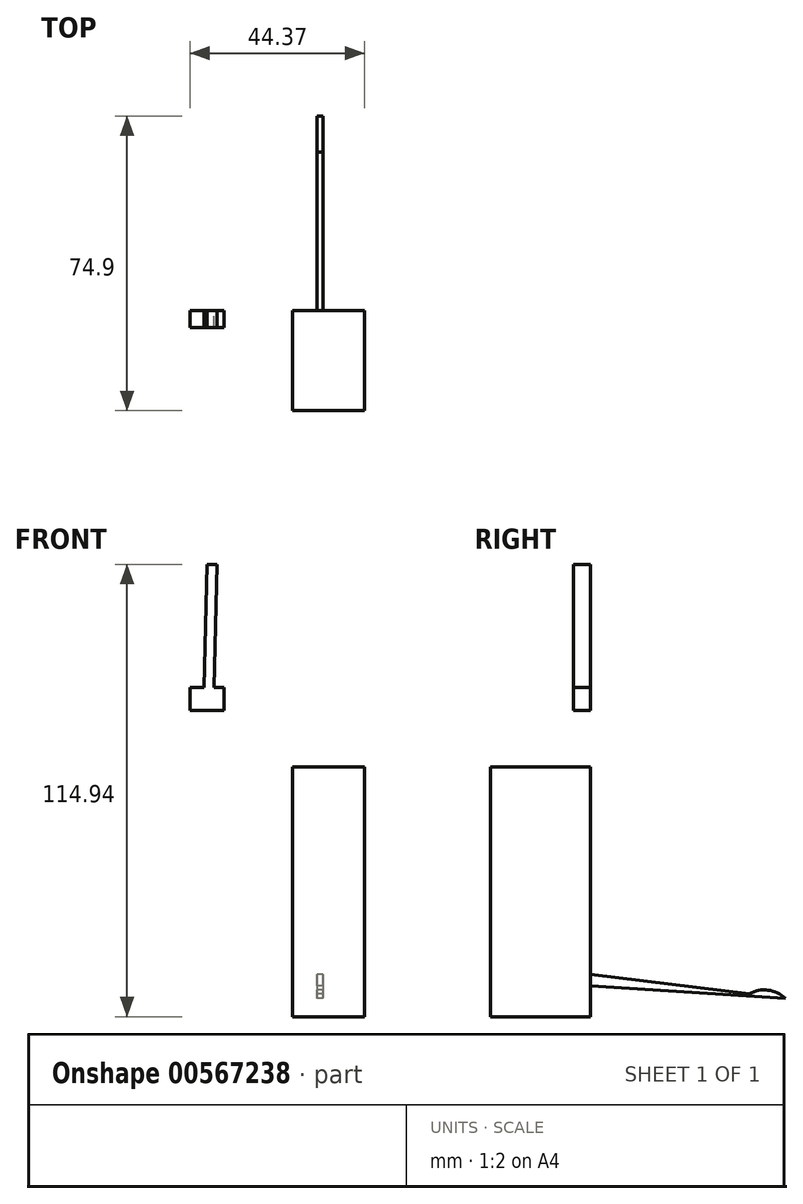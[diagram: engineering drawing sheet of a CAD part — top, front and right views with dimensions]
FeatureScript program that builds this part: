
annotation { "Feature Type Name" : "Feature", "Feature Type Description" : "" }
export const myFeature = defineFeature(function(context is Context, id is Id, definition is map)
    precondition{}
    {
        {
            var Q0;
            Q0=qCreatedBy(makeId("Front.planeOp"),FACE);
            var sketch = newSketch(context, id + "F0", { "sketchPlane" : qUnion([Q0])});
            skLineSegment(sketch, "E0.bottom", {"start": v(-3.6, 14.41) * mm, "end": v(5.04, 14.41) * mm});
            skLineSegment(sketch, "E0.top", {"start": v(-3.6, 14.77) * mm, "end": v(5.04, 14.77) * mm});
            skLineSegment(sketch, "E0.left", {"start": v(-3.6, 14.41) * mm, "end": v(-3.6, 14.77) * mm});
            skLineSegment(sketch, "E0.right", {"start": v(5.04, 14.41) * mm, "end": v(5.04, 14.77) * mm});
            skLineSegment(sketch, "E1.top", {"start": v(-3.6, 9) * mm, "end": v(5.04, 9) * mm});
            skLineSegment(sketch, "E1.left", {"start": v(-3.6, 14.77) * mm, "end": v(-3.6, 9) * mm});
            skLineSegment(sketch, "E1.right", {"start": v(5.04, 14.77) * mm, "end": v(5.04, 9) * mm});
            skLineSegment(sketch, "E2", {"start": v(0, 14.77) * mm, "end": v(0.72, 46.12) * mm});
            skPoint(sketch, "E2.endSnap0", {"position": v(0.72, 9) * mm});
            skLineSegment(sketch, "E3", {"start": v(0.72, 46.12) * mm, "end": v(3.23, 46.06) * mm});
            skLineSegment(sketch, "E4", {"start": v(3.23, 46.06) * mm, "end": v(2.51, 14.77) * mm});
            skSolve(sketch);
        }
        {
            var Q0;
            Q0 = qSketchRegion(id + "F0", true);
            extrude(context, id + "F1", {"entities" : qUnion([Q0]), "depth" : 4.32 * mm, "offsetDistance" : 25.4 * mm});
        }
        {
            var Q0;
            Q0=qCreatedBy(makeId("Front.planeOp"),FACE);
            var sketch = newSketch(context, id + "F2", { "sketchPlane" : qUnion([Q0])});
            skLineSegment(sketch, "E5.bottom", {"start": v(22.4, -5.4) * mm, "end": v(40.77, -5.4) * mm});
            skLineSegment(sketch, "E5.top", {"start": v(22.4, -68.82) * mm, "end": v(40.77, -68.82) * mm});
            skLineSegment(sketch, "E5.left", {"start": v(22.4, -5.4) * mm, "end": v(22.4, -68.82) * mm});
            skLineSegment(sketch, "E5.right", {"start": v(40.77, -5.4) * mm, "end": v(40.77, -68.82) * mm});
            skSolve(sketch);
        }
        {
            var Q0;
            Q0 = qSketchRegion(id + "F2", true);
            extrude(context, id + "F3", {"entities" : qUnion([Q0]), "depth" : 25.4 * mm, "offsetDistance" : 25.4 * mm});
        }
        {
            var Q0;
            Q0=qCreatedBy(makeId("Right.planeOp"),FACE);
            var sketch = newSketch(context, id + "F4", { "sketchPlane" : qUnion([Q0])});
            skLineSegment(sketch, "E6", {"start": v(0, -58.01) * mm, "end": v(0, -58.01) * mm});
            skLineSegment(sketch, "E7", {"start": v(0, -58.01) * mm, "end": v(40.34, -63.01) * mm});
            skLineSegment(sketch, "E8", {"start": v(49.5, -64.15) * mm, "end": v(49.5, -64.15) * mm});
            skArc(sketch, "E9", {"start": v(49.5, -64.15) * mm, "mid": v(45.1, -62.1) * mm, "end": v(40.34, -63.01) * mm});
            skLineSegment(sketch, "E10", {"start": v(0, -58.01) * mm, "end": v(-0.37, -60.98) * mm});
            skLineSegment(sketch, "E11", {"start": v(-0.37, -60.98) * mm, "end": v(49.5, -64.15) * mm});
            skSolve(sketch);
        }
        {
            var Q0;
            Q0 = qSketchRegion(id + "F4", true);
            extrude(context, id + "F5", {"entities" : qUnion([Q0]), "operationType" : NewBodyOperationType.ADD, "depth" : 30.23 * mm, "offsetDistance" : 25.4 * mm, "hasSecondDirection" : true, "secondDirectionOppositeDirection" : false, "secondDirectionDepth" : 28.7 * mm});
        }
    });
